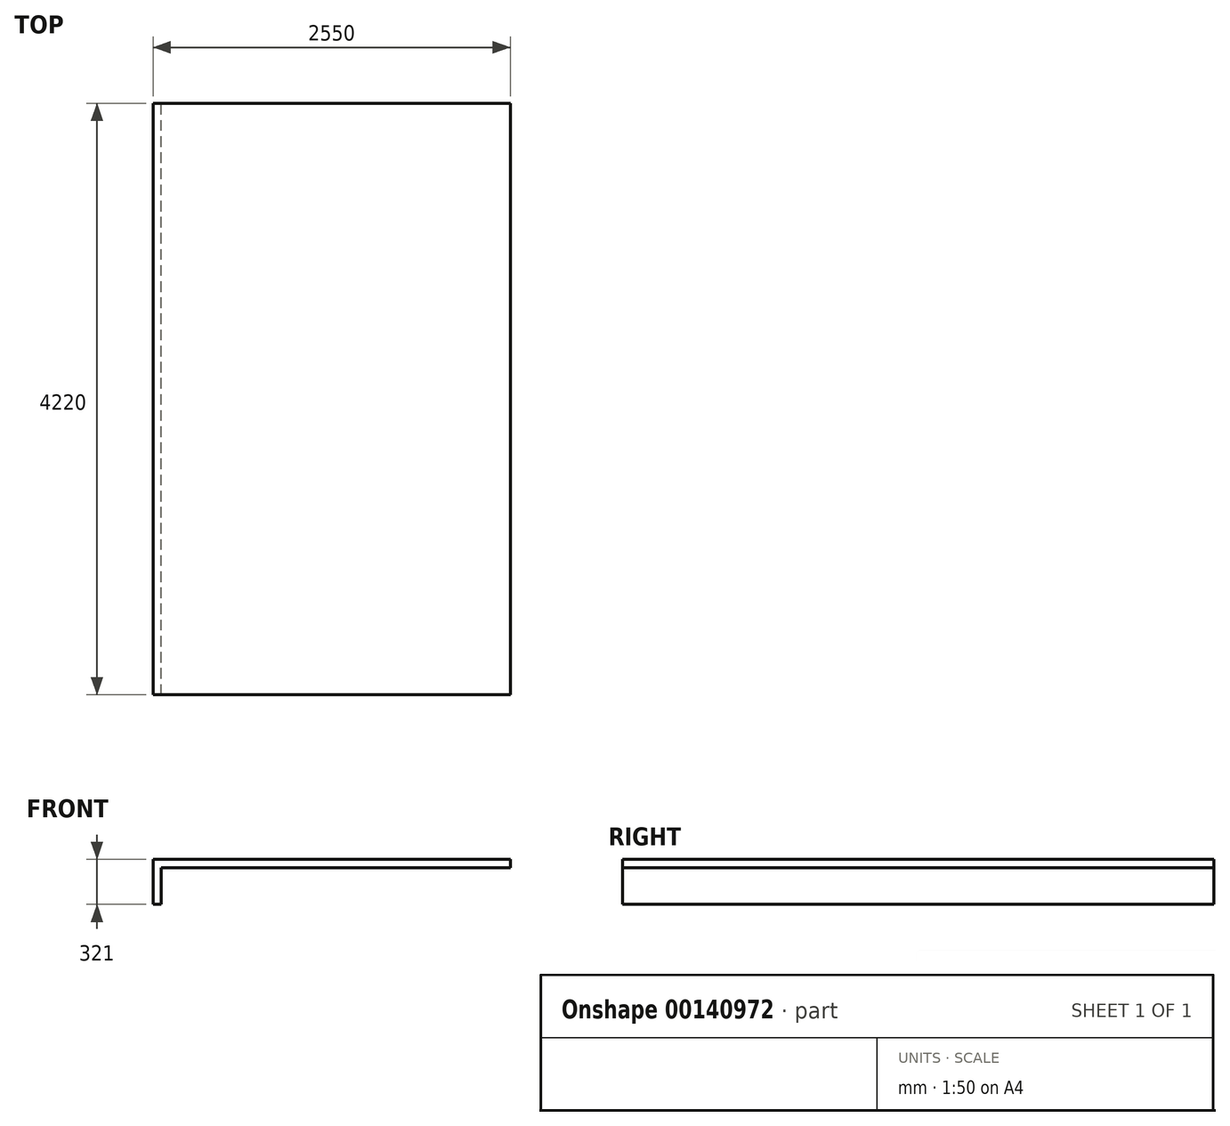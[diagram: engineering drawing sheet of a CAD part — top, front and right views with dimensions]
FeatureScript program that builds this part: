
annotation { "Feature Type Name" : "Feature", "Feature Type Description" : "" }
export const myFeature = defineFeature(function(context is Context, id is Id, definition is map)
    precondition{}
    {
        {
            var Q0;
            Q0=qCreatedBy(makeId("Front.planeOp"),FACE);
            var sketch = newSketch(context, id + "F0", { "sketchPlane" : qUnion([Q0])});
            skLineSegment(sketch, "E0", {"start": v(-1275, 0) * mm, "end": v(-1275, 321) * mm});
            skLineSegment(sketch, "E1", {"start": v(-1275, 321) * mm, "end": v(0, 321) * mm});
            skLineSegment(sketch, "E2", {"start": v(0, 0) * mm, "end": v(0, 321) * mm, "construction": true});
            skLineSegment(sketch, "E3.MirrorCS", {"start": v(1275, 321) * mm, "end": v(0, 321) * mm});
            skLineSegment(sketch, "E4.MirrorCS", {"start": v(1275, 0) * mm, "end": v(1275, 321) * mm, "construction": true});
            skLineSegment(sketch, "E5", {"start": v(-1275, 0) * mm, "end": v(-1215, 0) * mm});
            skLineSegment(sketch, "E6", {"start": v(-1215, 0) * mm, "end": v(-1215, 261) * mm});
            skLineSegment(sketch, "E7", {"start": v(-1215, 261) * mm, "end": v(0, 261) * mm});
            skLineSegment(sketch, "E8.MirrorCS", {"start": v(1215, 261) * mm, "end": v(0, 261) * mm});
            skLineSegment(sketch, "E9.MirrorCS", {"start": v(1215, 0) * mm, "end": v(1215, 261) * mm, "construction": true});
            skLineSegment(sketch, "E10", {"start": v(1215, 261) * mm, "end": v(1275, 261) * mm});
            skLineSegment(sketch, "E11", {"start": v(1275, 261) * mm, "end": v(1275, 321) * mm});
            skSolve(sketch);
        }
        {
            var Q0;
            Q0 = qSketchRegion(id + "F0", true);
            extrude(context, id + "F1", {"entities" : qUnion([Q0]), "depth" : 4220 * mm});
        }
    });
